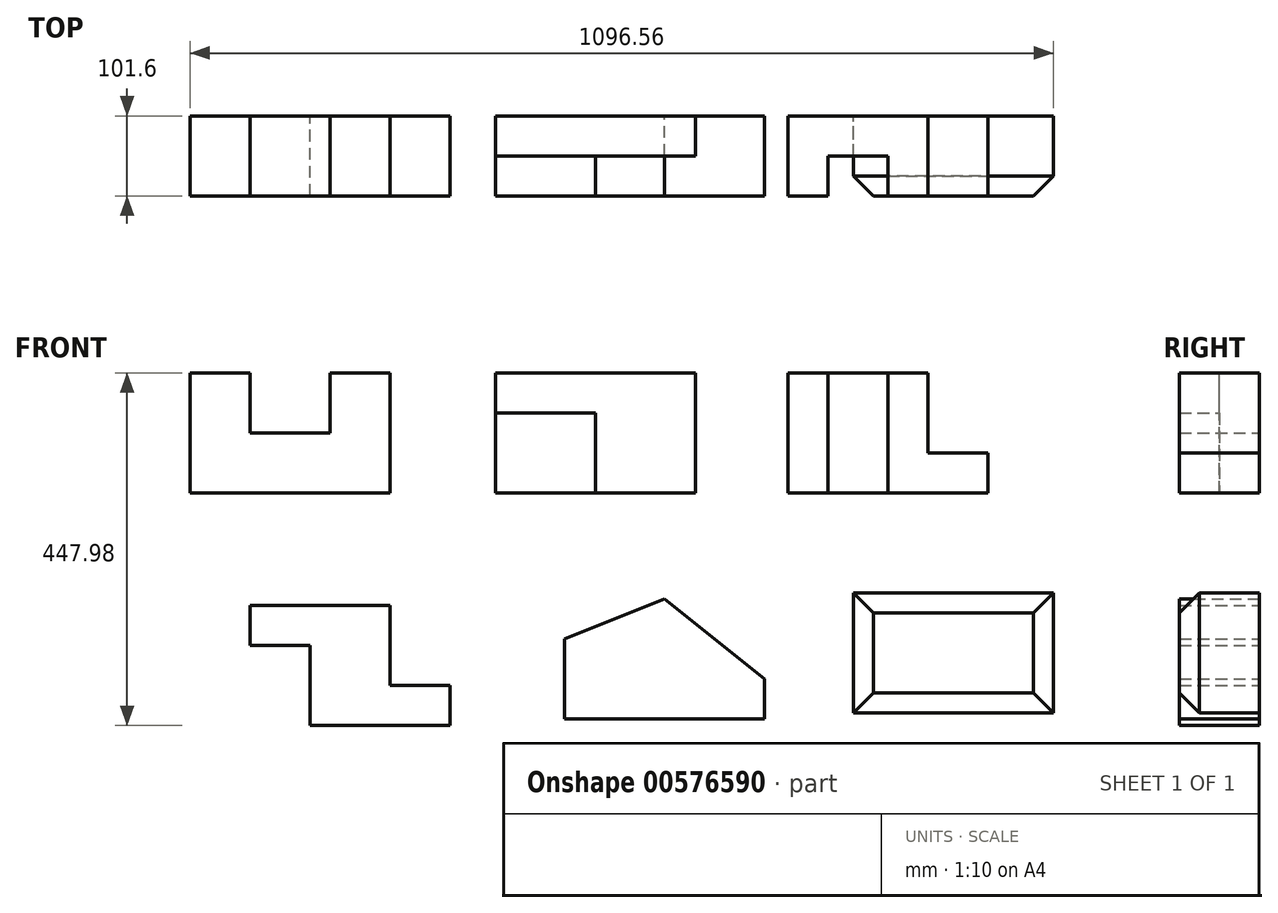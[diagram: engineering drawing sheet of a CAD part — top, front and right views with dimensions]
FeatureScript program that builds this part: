
annotation { "Feature Type Name" : "Feature", "Feature Type Description" : "" }
export const myFeature = defineFeature(function(context is Context, id is Id, definition is map)
    precondition{}
    {
        {
            var Q0;
            Q0=qCreatedBy(makeId("Front.planeOp"),FACE);
            var sketch = newSketch(context, id + "F0", { "sketchPlane" : qUnion([Q0])});
            skLineSegment(sketch, "E0", {"start": v(0, 0) * mm, "end": v(0, 152.4) * mm});
            skLineSegment(sketch, "E1", {"start": v(0, 152.4) * mm, "end": v(-76.2, 152.4) * mm});
            skLineSegment(sketch, "E2", {"start": v(-76.2, 152.4) * mm, "end": v(-76.2, 76.2) * mm});
            skLineSegment(sketch, "E3", {"start": v(-76.2, 76.2) * mm, "end": v(-177.8, 76.2) * mm});
            skLineSegment(sketch, "E4", {"start": v(-177.8, 76.2) * mm, "end": v(-177.8, 152.4) * mm});
            skLineSegment(sketch, "E5", {"start": v(-177.8, 152.4) * mm, "end": v(-254, 152.4) * mm});
            skLineSegment(sketch, "E6", {"start": v(-254, 152.4) * mm, "end": v(-254, 0) * mm});
            skLineSegment(sketch, "E7", {"start": v(-254, 0) * mm, "end": v(0, 0) * mm});
            skSolve(sketch);
        }
        {
            var Q0;
            Q0 = qSketchRegion(id + "F0", true);
            extrude(context, id + "F1", {"entities" : qUnion([Q0]), "depth" : 101.6 * mm, "offsetDistance" : 25.4 * mm});
        }
        {
            var Q0;
            Q0=qCreatedBy(makeId("Front.planeOp"),FACE);
            var sketch = newSketch(context, id + "F2", { "sketchPlane" : qUnion([Q0])});
            skLineSegment(sketch, "E8", {"start": v(133.77, 0) * mm, "end": v(260.77, 0) * mm});
            skLineSegment(sketch, "E9", {"start": v(133.77, 0) * mm, "end": v(133.77, 101.6) * mm});
            skLineSegment(sketch, "E10", {"start": v(133.77, 101.6) * mm, "end": v(260.77, 101.6) * mm});
            skLineSegment(sketch, "E11", {"start": v(260.77, 101.6) * mm, "end": v(260.77, 0) * mm});
            skLineSegment(sketch, "E12", {"start": v(260.77, 0) * mm, "end": v(387.77, 0) * mm});
            skLineSegment(sketch, "E13", {"start": v(387.77, 0) * mm, "end": v(387.77, 152.4) * mm});
            skLineSegment(sketch, "E14", {"start": v(387.77, 152.4) * mm, "end": v(133.77, 152.4) * mm});
            skLineSegment(sketch, "E15", {"start": v(133.77, 152.4) * mm, "end": v(133.77, 101.6) * mm});
            skSolve(sketch);
        }
        {
            var Q0;
            Q0 = qSketchRegion(id + "F0", true);
            extrude(context, id + "F3", {"entities" : qUnion([Q0]), "operationType" : NewBodyOperationType.ADD, "depth" : 101.6 * mm, "offsetDistance" : 25.4 * mm});
        }
        {
            var Q0;
            Q0=makeQuery(id+"F2.imprint","IMPRINT",FACE,{"disambiguationData":[TD([[makeQuery(id+"F2.imprint","IMPRINT",EDGE,{"derivedFrom":sQuery(id+"F2.wireOp",EDGE,"E8")}),1.0]])]});
            extrude(context, id + "F4", {"entities" : qUnion([Q0]), "depth" : 101.6 * mm, "offsetDistance" : 25.4 * mm});
        }
        {
            var Q0;
            Q0 = qSketchRegion(id + "F2", true);
            extrude(context, id + "F5", {"entities" : qUnion([Q0]), "operationType" : NewBodyOperationType.ADD, "depth" : 50.8 * mm, "offsetDistance" : 25.4 * mm});
        }
        {
            var Q0;
            Q0=qCreatedBy(makeId("Front.planeOp"),FACE);
            var sketch = newSketch(context, id + "F6", { "sketchPlane" : qUnion([Q0])});
            skLineSegment(sketch, "E16", {"start": v(505.1, 0) * mm, "end": v(505.1, 152.4) * mm});
            skLineSegment(sketch, "E17", {"start": v(505.1, 152.4) * mm, "end": v(555.9, 152.4) * mm});
            skLineSegment(sketch, "E18", {"start": v(555.9, 152.4) * mm, "end": v(555.9, 0) * mm});
            skLineSegment(sketch, "E19", {"start": v(555.9, 0) * mm, "end": v(505.1, 0) * mm});
            skLineSegment(sketch, "E20", {"start": v(555.9, 0) * mm, "end": v(632.1, 0) * mm});
            skLineSegment(sketch, "E21", {"start": v(632.1, 152.4) * mm, "end": v(555.9, 152.4) * mm});
            skLineSegment(sketch, "E22", {"start": v(632.1, 152.4) * mm, "end": v(632.1, 0) * mm});
            skPoint(sketch, "E23.end.orphan", {"position": v(682.9, 152.4) * mm});
            skPoint(sketch, "E24.start.orphan", {"position": v(759.1, 0) * mm});
            skLineSegment(sketch, "E25", {"start": v(682.9, 152.4) * mm, "end": v(632.1, 152.4) * mm});
            skLineSegment(sketch, "E26", {"start": v(632.1, 0) * mm, "end": v(759.1, 0) * mm});
            skLineSegment(sketch, "E27", {"start": v(759.1, 0) * mm, "end": v(759.1, 50.8) * mm});
            skLineSegment(sketch, "E28", {"start": v(759.1, 50.8) * mm, "end": v(682.9, 50.8) * mm});
            skLineSegment(sketch, "E29", {"start": v(682.9, 50.8) * mm, "end": v(682.9, 152.4) * mm});
            skSolve(sketch);
        }
        {
            var Q0;
            Q0=makeQuery(id+"F6.imprint","IMPRINT",FACE,{"disambiguationData":[TD([[makeQuery(id+"F6.imprint","IMPRINT",EDGE,{"derivedFrom":sQuery(id+"F6.wireOp",EDGE,"E16")}),-1.0]])]});
            extrude(context, id + "F7", {"entities" : qUnion([Q0]), "depth" : 101.6 * mm, "offsetDistance" : 25.4 * mm});
        }
        {
            var Q0;
            Q0 = qSketchRegion(id + "F6", true);
            extrude(context, id + "F8", {"entities" : qUnion([Q0]), "operationType" : NewBodyOperationType.ADD, "depth" : 50.8 * mm, "offsetDistance" : 25.4 * mm});
        }
        {
            var Q0;
            Q0=makeQuery(id+"F6.imprint","IMPRINT",FACE,{"disambiguationData":[TD([[makeQuery(id+"F6.imprint","IMPRINT",EDGE,{"derivedFrom":sQuery(id+"F6.wireOp",EDGE,"E22")}),1.0]])]});
            extrude(context, id + "F9", {"entities" : qUnion([Q0]), "operationType" : NewBodyOperationType.ADD, "depth" : 101.6 * mm, "offsetDistance" : 25.4 * mm});
        }
        {
            var Q0;
            Q0=qCreatedBy(makeId("Front.planeOp"),FACE);
            var sketch = newSketch(context, id + "F10", { "sketchPlane" : qUnion([Q0])});
            skLineSegment(sketch, "E30", {"start": v(0, -143.18) * mm, "end": v(-177.8, -143.18) * mm});
            skLineSegment(sketch, "E31", {"start": v(-177.8, -143.18) * mm, "end": v(-177.8, -193.98) * mm});
            skLineSegment(sketch, "E32", {"start": v(-177.8, -193.98) * mm, "end": v(-101.6, -193.98) * mm});
            skLineSegment(sketch, "E33", {"start": v(-101.6, -193.98) * mm, "end": v(-101.6, -295.58) * mm});
            skLineSegment(sketch, "E34", {"start": v(-101.6, -295.58) * mm, "end": v(76.2, -295.58) * mm});
            skLineSegment(sketch, "E35", {"start": v(76.2, -295.58) * mm, "end": v(76.2, -244.78) * mm});
            skLineSegment(sketch, "E36", {"start": v(76.2, -244.78) * mm, "end": v(0, -244.78) * mm});
            skLineSegment(sketch, "E37", {"start": v(0, -244.78) * mm, "end": v(0, -143.18) * mm});
            skSolve(sketch);
        }
        {
            var Q0;
            Q0 = qSketchRegion(id + "F10", true);
            extrude(context, id + "F11", {"entities" : qUnion([Q0]), "depth" : 101.6 * mm, "offsetDistance" : 25.4 * mm});
        }
        {
            var Q0;
            Q0=qCreatedBy(makeId("Front.planeOp"),FACE);
            var sketch = newSketch(context, id + "F12", { "sketchPlane" : qUnion([Q0])});
            skLineSegment(sketch, "E38", {"start": v(221.76, -286.92) * mm, "end": v(221.76, -185.32) * mm});
            skLineSegment(sketch, "E39", {"start": v(221.76, -286.92) * mm, "end": v(475.76, -286.92) * mm});
            skLineSegment(sketch, "E40", {"start": v(475.76, -286.92) * mm, "end": v(475.76, -236.12) * mm});
            skLineSegment(sketch, "E41", {"start": v(221.76, -286.92) * mm, "end": v(348.76, -286.92) * mm});
            skLineSegment(sketch, "E42", {"start": v(348.76, -286.92) * mm, "end": v(348.76, -134.52) * mm});
            skLineSegment(sketch, "E43", {"start": v(221.76, -185.32) * mm, "end": v(348.76, -134.52) * mm});
            skLineSegment(sketch, "E44", {"start": v(475.76, -236.12) * mm, "end": v(348.76, -134.52) * mm});
            skSolve(sketch);
        }
        {
            var Q0;
            Q0=makeQuery(id+"F12.imprint","IMPRINT",FACE,{"disambiguationData":[TD([[makeQuery(id+"F12.imprint","IMPRINT",EDGE,{"derivedFrom":sQuery(id+"F12.wireOp",EDGE,"E39")}),1.0]])]});
            var Q1;
            Q1=makeQuery(id+"F12.imprint","IMPRINT",FACE,{"disambiguationData":[TD([[makeQuery(id+"F12.imprint","IMPRINT",EDGE,{"derivedFrom":sQuery(id+"F12.wireOp",EDGE,"E38")}),-1.0]])]});
            extrude(context, id + "F13", {"entities" : qUnion([Q0, Q1]), "depth" : 101.6 * mm, "offsetDistance" : 25.4 * mm});
        }
        {
            var Q0;
            Q0=qCreatedBy(makeId("Front.planeOp"),FACE);
            var sketch = newSketch(context, id + "F14", { "sketchPlane" : qUnion([Q0])});
            skLineSegment(sketch, "E45", {"start": v(588.56, -279.6) * mm, "end": v(588.56, -127.2) * mm});
            skLineSegment(sketch, "E46", {"start": v(588.56, -127.2) * mm, "end": v(842.56, -127.2) * mm});
            skLineSegment(sketch, "E47", {"start": v(842.56, -127.2) * mm, "end": v(842.56, -279.6) * mm});
            skLineSegment(sketch, "E48", {"start": v(588.56, -279.6) * mm, "end": v(842.56, -279.6) * mm});
            skSolve(sketch);
        }
        {
            var Q0;
            Q0 = qSketchRegion(id + "F14", true);
            extrude(context, id + "F15", {"entities" : qUnion([Q0]), "depth" : 101.6 * mm, "offsetDistance" : 25.4 * mm});
        }
        {
            var Q0;
            Q0=makeQuery(id+"F15.opExtrude","CAP_FACE",FACE,{"disambiguationData":[OSD([sQuery(id+"F14.wireOp",EDGE,"E45"),sQuery(id+"F14.wireOp",EDGE,"E46"),sQuery(id+"F14.wireOp",EDGE,"E47"),sQuery(id+"F14.wireOp",EDGE,"E48")])],"isStart":false});
            chamfer(context, id + "F16", {"entities" : qUnion([Q0]), "chamferType" : ChamferType.OFFSET_ANGLE, "width" : 25.4 * mm, "oppositeDirection" : false, "angle" : 45 * degree, "tangentPropagation" : true});
        }
    });
